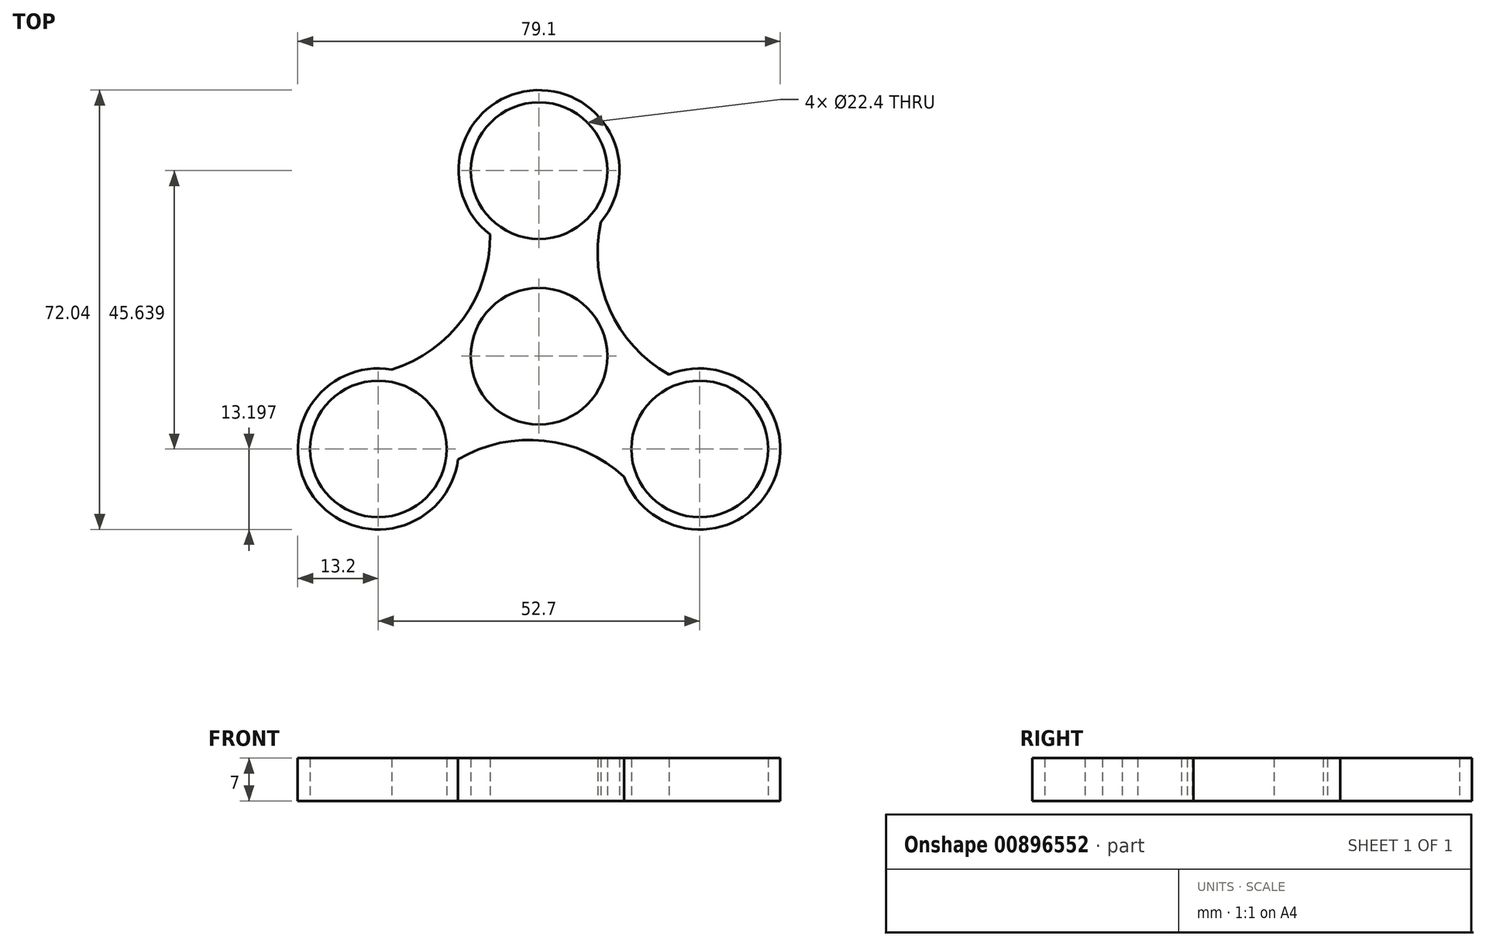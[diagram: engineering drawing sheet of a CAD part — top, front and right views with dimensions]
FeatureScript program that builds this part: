
annotation { "Feature Type Name" : "Feature", "Feature Type Description" : "" }
export const myFeature = defineFeature(function(context is Context, id is Id, definition is map)
    precondition{}
    {
        {
            var Q0;
            Q0=qCreatedBy(makeId("Top.planeOp"),FACE);
            var sketch = newSketch(context, id + "F0", { "sketchPlane" : qUnion([Q0])});
            skCircle(sketch, "E0", {"center": v(0, 0) * mm, "radius": 11.2 * mm});
            skCircle(sketch, "E1", {"center": v(0, 0) * mm, "radius": 13.2 * mm});
            skCircle(sketch, "E2", {"center": v(0, 30.43) * mm, "radius": 11.2 * mm});
            skCircle(sketch, "E3", {"center": v(0, 30.43) * mm, "radius": 13.2 * mm});
            skCircle(sketch, "E4.1.0", {"center": v(-26.35, -15.21) * mm, "radius": 11.2 * mm});
            skCircle(sketch, "E4.1.1", {"center": v(-26.35, -15.21) * mm, "radius": 13.2 * mm});
            skCircle(sketch, "E4.2.0", {"center": v(26.35, -15.21) * mm, "radius": 11.2 * mm});
            skCircle(sketch, "E4.2.1", {"center": v(26.35, -15.21) * mm, "radius": 13.2 * mm});
            skArc(sketch, "E5", {"start": v(10.17, 22.01) * mm, "mid": v(12.21, 6.34) * mm, "end": v(23.91, -4.28) * mm});
            skArc(sketch, "E6.1.0", {"start": v(-24.15, -2.2) * mm, "mid": v(-11.6, 7.4) * mm, "end": v(-8.25, 22.85) * mm});
            skArc(sketch, "E6.2.0", {"start": v(13.98, -19.81) * mm, "mid": v(-0.62, -13.74) * mm, "end": v(-15.66, -18.57) * mm});
            skSolve(sketch);
        }
        {
            var Q0;
            Q0=makeQuery(id+"F0.imprint","IMPRINT",FACE,{"disambiguationData":[TD([[makeQuery(id+"F0.imprint","IMPRINT",EDGE,{"derivedFrom":sQuery(id+"F0.wireOp",EDGE,"E4.1.0")}),-1.0]])]});
            var Q1;
            Q1=makeQuery(id+"F0.imprint","IMPRINT",FACE,{"disambiguationData":[TD([[makeQuery(id+"F0.imprint","IMPRINT",EDGE,{"derivedFrom":sQuery(id+"F0.wireOp",EDGE,"E4.2.0")}),-1.0]])]});
            var Q2;
            Q2=makeQuery(id+"F0.imprint","IMPRINT",FACE,{"disambiguationData":[TD([[makeQuery(id+"F0.imprint","IMPRINT",EDGE,{"derivedFrom":sQuery(id+"F0.wireOp",EDGE,"E0")}),-1.0]])]});
            var Q3;
            Q3=makeQuery(id+"F0.imprint","IMPRINT",FACE,{"disambiguationData":[TD([[makeQuery(id+"F0.imprint","IMPRINT",EDGE,{"derivedFrom":sQuery(id+"F0.wireOp",EDGE,"E2")}),-1.0]])]});
            var Q4;
            Q4=makeQuery(id+"F0.imprint","IMPRINT",FACE,{"disambiguationData":[TD([[makeQuery(id+"F0.imprint","IMPRINT",EDGE,{"derivedFrom":sQuery(id+"F0.wireOp",EDGE,"E1")}),-1.0]])]});
            extrude(context, id + "F1", {"entities" : qUnion([Q0, Q1, Q2, Q3, Q4]), "depth" : 7 * mm, "offsetDistance" : 25 * mm});
        }
    });
